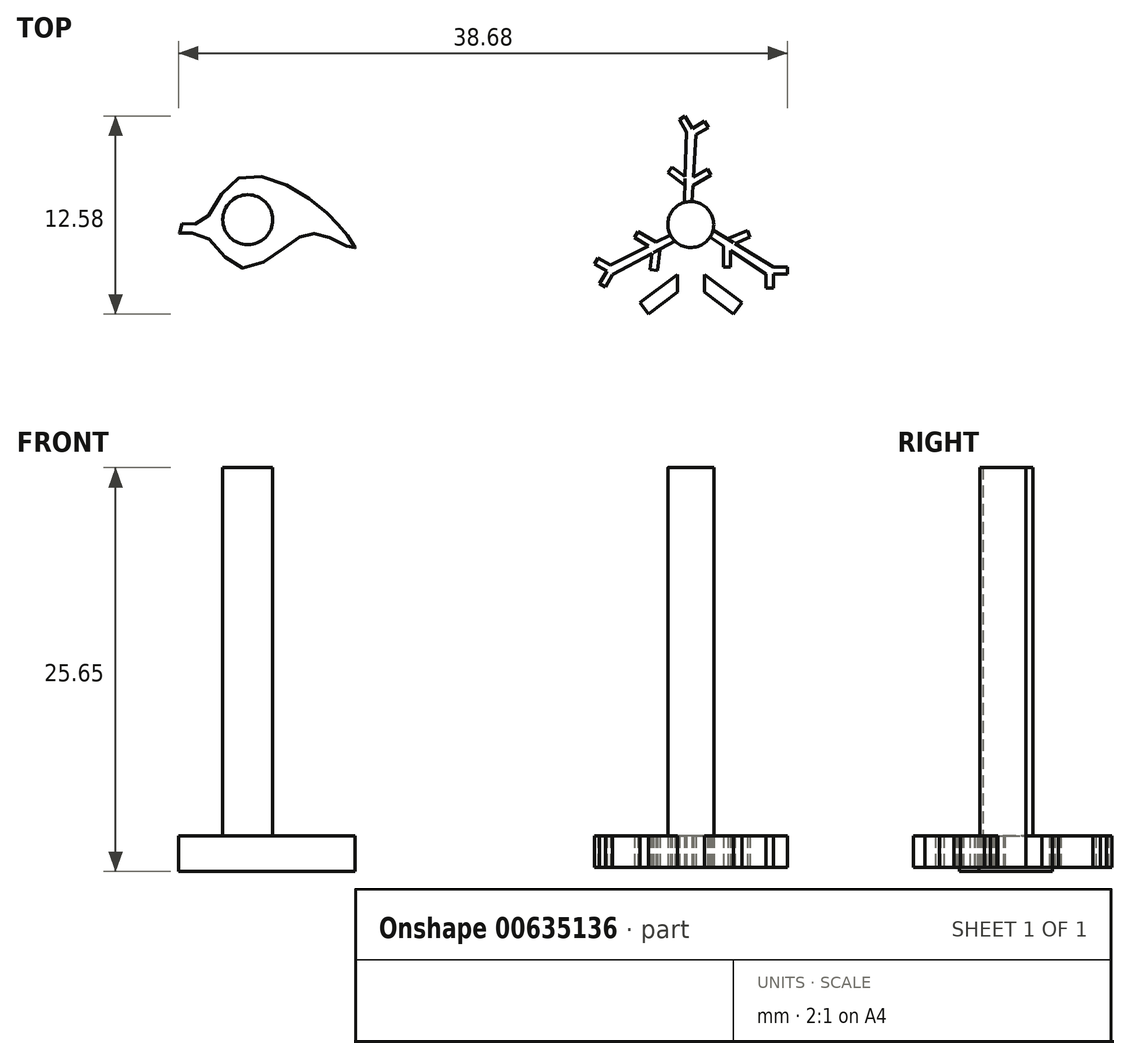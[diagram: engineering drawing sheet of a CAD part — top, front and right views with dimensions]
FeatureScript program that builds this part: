
annotation { "Feature Type Name" : "Feature", "Feature Type Description" : "" }
export const myFeature = defineFeature(function(context is Context, id is Id, definition is map)
    precondition{}
    {
        {
            var Q0;
            Q0=qCreatedBy(makeId("Top.planeOp"),FACE);
            var sketch = newSketch(context, id + "F0", { "sketchPlane" : qUnion([Q0])});
            skLineSegment(sketch, "E0.bottom", {"start": v(-0.85, 0) * mm, "end": v(0.86, 0) * mm});
            skLineSegment(sketch, "E0.top", {"start": v(-0.85, -6.35) * mm, "end": v(0.86, -6.35) * mm});
            skLineSegment(sketch, "E0.left", {"start": v(-0.85, 0) * mm, "end": v(-0.85, -6.35) * mm});
            skLineSegment(sketch, "E0.right", {"start": v(0.86, 0) * mm, "end": v(0.86, -6.35) * mm});
            skLineSegment(sketch, "E1", {"start": v(-0.85, -3.17) * mm, "end": v(-3.24, -4.96) * mm});
            skLineSegment(sketch, "E2", {"start": v(-3.24, -4.96) * mm, "end": v(-2.7, -5.69) * mm});
            skLineSegment(sketch, "E3", {"start": v(-2.7, -5.69) * mm, "end": v(-0.85, -4.3) * mm});
            skLineSegment(sketch, "E4", {"start": v(-0.85, -4.3) * mm, "end": v(-0.85, -3.17) * mm});
            skLineSegment(sketch, "E5", {"start": v(0, 0) * mm, "end": v(0, -6.35) * mm, "construction": true});
            skLineSegment(sketch, "E6.MirrorCS", {"start": v(2.71, -5.69) * mm, "end": v(0.86, -4.3) * mm});
            skLineSegment(sketch, "E7.MirrorCS", {"start": v(3.25, -4.96) * mm, "end": v(2.71, -5.69) * mm});
            skLineSegment(sketch, "E8.MirrorCS", {"start": v(0.86, -3.17) * mm, "end": v(3.25, -4.96) * mm});
            skLineSegment(sketch, "E9.MirrorCS", {"start": v(0.86, -4.3) * mm, "end": v(0.86, -3.17) * mm});
            skLineSegment(sketch, "E10.MirrorCS", {"start": v(0.86, 0) * mm, "end": v(-0.85, 0) * mm});
            skLineSegment(sketch, "E11.MirrorCS", {"start": v(0.86, -6.35) * mm, "end": v(-0.85, -6.35) * mm});
            skLineSegment(sketch, "E12", {"start": v(0, 0) * mm, "end": v(4.78, -3.14) * mm});
            skLineSegment(sketch, "E13", {"start": v(4.78, -3.14) * mm, "end": v(4.78, -4.05) * mm});
            skLineSegment(sketch, "E14", {"start": v(4.78, -4.05) * mm, "end": v(5.24, -4.05) * mm});
            skLineSegment(sketch, "E15", {"start": v(5.24, -4.05) * mm, "end": v(5.24, -3.14) * mm});
            skLineSegment(sketch, "E16", {"start": v(5.24, -3.14) * mm, "end": v(6.15, -3.14) * mm});
            skLineSegment(sketch, "E17", {"start": v(6.15, -3.14) * mm, "end": v(6.15, -2.7) * mm});
            skLineSegment(sketch, "E18", {"start": v(6.15, -2.7) * mm, "end": v(5.24, -2.7) * mm});
            skLineSegment(sketch, "E19", {"start": v(5.24, -2.7) * mm, "end": v(0.86, 0) * mm});
            skLineSegment(sketch, "E20", {"start": v(2.06, -1.35) * mm, "end": v(2.06, -2.68) * mm});
            skLineSegment(sketch, "E21", {"start": v(2.06, -2.68) * mm, "end": v(2.52, -2.68) * mm});
            skLineSegment(sketch, "E22", {"start": v(2.52, -2.68) * mm, "end": v(2.52, -1.65) * mm});
            skLineSegment(sketch, "E23", {"start": v(0.51, 0) * mm, "end": v(5.24, -3.14) * mm, "construction": true});
            skLineSegment(sketch, "E24.MirrorCS", {"start": v(3.76, -0.8) * mm, "end": v(2.8, -1.2) * mm});
            skLineSegment(sketch, "E25.MirrorCS", {"start": v(3.59, -0.39) * mm, "end": v(3.76, -0.8) * mm});
            skLineSegment(sketch, "E26.MirrorCS", {"start": v(2.36, -0.9) * mm, "end": v(3.59, -0.39) * mm});
            skLineSegment(sketch, "E27", {"start": v(2.36, -0.9) * mm, "end": v(2.8, -1.2) * mm});
            skLineSegment(sketch, "E28.1.0", {"start": v(0.33, 5.71) * mm, "end": v(1.11, 6.17) * mm});
            skLineSegment(sketch, "E28.1.1", {"start": v(0, 0) * mm, "end": v(5.5, 3.18) * mm, "construction": true});
            skLineSegment(sketch, "E28.1.2", {"start": v(2.32, 2.34) * mm, "end": v(2.67, 5.3) * mm});
            skLineSegment(sketch, "E28.1.3", {"start": v(0.14, 2.46) * mm, "end": v(1.3, 3.13) * mm});
            skLineSegment(sketch, "E28.1.4", {"start": v(1.07, 3.52) * mm, "end": v(0.17, 3) * mm});
            skLineSegment(sketch, "E28.1.5", {"start": v(3.57, 5.2) * mm, "end": v(3.3, 2.9) * mm});
            skLineSegment(sketch, "E28.1.6", {"start": v(-1.18, 3.66) * mm, "end": v(-0.36, 3.04) * mm});
            skLineSegment(sketch, "E28.1.7", {"start": v(-0.43, 0.75) * mm, "end": v(5.07, 3.92) * mm});
            skLineSegment(sketch, "E28.1.8", {"start": v(0, 0) * mm, "end": v(0.33, 5.71) * mm});
            skLineSegment(sketch, "E28.1.9", {"start": v(0.43, -0.74) * mm, "end": v(5.92, 2.44) * mm});
            skLineSegment(sketch, "E28.1.10", {"start": v(-0.4, 2.5) * mm, "end": v(-1.46, 3.3) * mm});
            skLineSegment(sketch, "E28.1.11", {"start": v(3.3, 2.9) * mm, "end": v(2.32, 2.34) * mm});
            skLineSegment(sketch, "E28.1.12", {"start": v(2.67, 5.3) * mm, "end": v(3.57, 5.2) * mm});
            skLineSegment(sketch, "E28.1.13", {"start": v(-0.26, 0.44) * mm, "end": v(0.1, 6.1) * mm, "construction": true});
            skLineSegment(sketch, "E28.1.14", {"start": v(3.18, 0.85) * mm, "end": v(5.92, -0.33) * mm});
            skLineSegment(sketch, "E28.1.15", {"start": v(0.1, 6.1) * mm, "end": v(-0.36, 6.9) * mm});
            skLineSegment(sketch, "E28.1.16", {"start": v(-0.28, 5.89) * mm, "end": v(-0.43, 0.75) * mm});
            skLineSegment(sketch, "E28.1.17", {"start": v(0.88, 6.56) * mm, "end": v(0.1, 6.1) * mm});
            skLineSegment(sketch, "E28.1.18", {"start": v(0.43, -0.74) * mm, "end": v(-0.43, 0.75) * mm});
            skLineSegment(sketch, "E28.1.19", {"start": v(5.92, 2.44) * mm, "end": v(5.07, 3.92) * mm});
            skLineSegment(sketch, "E28.1.20", {"start": v(5.92, -0.33) * mm, "end": v(6.27, 0.5) * mm});
            skLineSegment(sketch, "E28.1.21", {"start": v(-0.73, 6.67) * mm, "end": v(-0.28, 5.89) * mm});
            skLineSegment(sketch, "E28.1.22", {"start": v(6.27, 0.5) * mm, "end": v(4.15, 1.41) * mm});
            skLineSegment(sketch, "E28.1.23", {"start": v(5.92, -0.33) * mm, "end": v(6.27, 0.5) * mm});
            skLineSegment(sketch, "E28.1.24", {"start": v(3.57, 5.2) * mm, "end": v(3.3, 2.9) * mm});
            skLineSegment(sketch, "E28.1.25", {"start": v(6.27, 0.5) * mm, "end": v(4.15, 1.41) * mm});
            skLineSegment(sketch, "E28.1.26", {"start": v(2.67, 5.3) * mm, "end": v(3.57, 5.2) * mm});
            skLineSegment(sketch, "E28.1.27", {"start": v(4.15, 1.41) * mm, "end": v(3.18, 0.85) * mm});
            skLineSegment(sketch, "E28.1.28", {"start": v(-0.43, 0.75) * mm, "end": v(0.43, -0.74) * mm});
            skLineSegment(sketch, "E28.1.29", {"start": v(2.32, 2.34) * mm, "end": v(2.67, 5.3) * mm});
            skLineSegment(sketch, "E28.1.30", {"start": v(5.07, 3.92) * mm, "end": v(5.92, 2.44) * mm});
            skLineSegment(sketch, "E28.1.31", {"start": v(-0.43, 0.75) * mm, "end": v(5.07, 3.92) * mm});
            skLineSegment(sketch, "E28.1.32", {"start": v(3.18, 0.85) * mm, "end": v(5.92, -0.33) * mm});
            skLineSegment(sketch, "E28.1.33", {"start": v(3.3, 2.9) * mm, "end": v(2.32, 2.34) * mm});
            skLineSegment(sketch, "E28.1.34", {"start": v(0.43, -0.74) * mm, "end": v(5.92, 2.44) * mm});
            skLineSegment(sketch, "E28.1.35", {"start": v(4.15, 1.41) * mm, "end": v(3.18, 0.85) * mm});
            skLineSegment(sketch, "E28.1.36", {"start": v(1.3, 3.13) * mm, "end": v(1.07, 3.52) * mm});
            skLineSegment(sketch, "E28.1.37", {"start": v(-0.4, 2.5) * mm, "end": v(-0.36, 3.04) * mm});
            skLineSegment(sketch, "E28.1.38", {"start": v(1.11, 6.17) * mm, "end": v(0.88, 6.56) * mm});
            skLineSegment(sketch, "E28.1.39", {"start": v(-0.36, 6.9) * mm, "end": v(-0.73, 6.67) * mm});
            skLineSegment(sketch, "E28.1.40", {"start": v(-1.46, 3.3) * mm, "end": v(-1.18, 3.66) * mm});
            skLineSegment(sketch, "E28.2.0", {"start": v(-5.1, -2.57) * mm, "end": v(-5.9, -2.12) * mm});
            skLineSegment(sketch, "E28.2.1", {"start": v(0, 0) * mm, "end": v(-5.5, 3.17) * mm, "construction": true});
            skLineSegment(sketch, "E28.2.2", {"start": v(-3.18, 0.84) * mm, "end": v(-5.93, -0.34) * mm});
            skLineSegment(sketch, "E28.2.3", {"start": v(-2.2, -1.11) * mm, "end": v(-3.36, -0.44) * mm});
            skLineSegment(sketch, "E28.2.4", {"start": v(-3.58, -0.84) * mm, "end": v(-2.69, -1.36) * mm});
            skLineSegment(sketch, "E28.2.5", {"start": v(-6.28, 0.5) * mm, "end": v(-4.16, 1.4) * mm});
            skLineSegment(sketch, "E28.2.6", {"start": v(-2.58, -2.86) * mm, "end": v(-2.45, -1.83) * mm});
            skLineSegment(sketch, "E28.2.7", {"start": v(-0.43, -0.75) * mm, "end": v(-5.93, 2.43) * mm});
            skLineSegment(sketch, "E28.2.8", {"start": v(0, 0) * mm, "end": v(-5.1, -2.57) * mm});
            skLineSegment(sketch, "E28.2.9", {"start": v(0.43, 0.74) * mm, "end": v(-5.07, 3.91) * mm});
            skLineSegment(sketch, "E28.2.10", {"start": v(-1.96, -1.6) * mm, "end": v(-2.13, -2.91) * mm});
            skLineSegment(sketch, "E28.2.11", {"start": v(-4.16, 1.4) * mm, "end": v(-3.18, 0.84) * mm});
            skLineSegment(sketch, "E28.2.12", {"start": v(-5.93, -0.34) * mm, "end": v(-6.28, 0.5) * mm});
            skLineSegment(sketch, "E28.2.13", {"start": v(-0.26, -0.44) * mm, "end": v(-5.34, -2.97) * mm, "construction": true});
            skLineSegment(sketch, "E28.2.14", {"start": v(-2.32, 2.32) * mm, "end": v(-2.68, 5.29) * mm});
            skLineSegment(sketch, "E28.2.15", {"start": v(-5.34, -2.97) * mm, "end": v(-5.8, -3.75) * mm});
            skLineSegment(sketch, "E28.2.16", {"start": v(-4.96, -3.18) * mm, "end": v(-0.43, -0.75) * mm});
            skLineSegment(sketch, "E28.2.17", {"start": v(-6.12, -2.51) * mm, "end": v(-5.34, -2.97) * mm});
            skLineSegment(sketch, "E28.2.18", {"start": v(0.43, 0.74) * mm, "end": v(-0.43, -0.75) * mm});
            skLineSegment(sketch, "E28.2.19", {"start": v(-5.07, 3.91) * mm, "end": v(-5.93, 2.43) * mm});
            skLineSegment(sketch, "E28.2.20", {"start": v(-2.68, 5.29) * mm, "end": v(-3.57, 5.18) * mm});
            skLineSegment(sketch, "E28.2.21", {"start": v(-5.41, -3.97) * mm, "end": v(-4.96, -3.18) * mm});
            skLineSegment(sketch, "E28.2.22", {"start": v(-3.57, 5.18) * mm, "end": v(-3.3, 2.89) * mm});
            skLineSegment(sketch, "E28.2.23", {"start": v(-2.68, 5.29) * mm, "end": v(-3.57, 5.18) * mm});
            skLineSegment(sketch, "E28.2.24", {"start": v(-6.28, 0.5) * mm, "end": v(-4.16, 1.4) * mm});
            skLineSegment(sketch, "E28.2.25", {"start": v(-3.57, 5.18) * mm, "end": v(-3.3, 2.89) * mm});
            skLineSegment(sketch, "E28.2.26", {"start": v(-5.93, -0.34) * mm, "end": v(-6.28, 0.5) * mm});
            skLineSegment(sketch, "E28.2.27", {"start": v(-3.3, 2.89) * mm, "end": v(-2.32, 2.32) * mm});
            skLineSegment(sketch, "E28.2.28", {"start": v(-0.43, -0.75) * mm, "end": v(0.43, 0.74) * mm});
            skLineSegment(sketch, "E28.2.29", {"start": v(-3.18, 0.84) * mm, "end": v(-5.93, -0.34) * mm});
            skLineSegment(sketch, "E28.2.30", {"start": v(-5.93, 2.43) * mm, "end": v(-5.07, 3.91) * mm});
            skLineSegment(sketch, "E28.2.31", {"start": v(-0.43, -0.75) * mm, "end": v(-5.93, 2.43) * mm});
            skLineSegment(sketch, "E28.2.32", {"start": v(-2.32, 2.32) * mm, "end": v(-2.68, 5.29) * mm});
            skLineSegment(sketch, "E28.2.33", {"start": v(-4.16, 1.4) * mm, "end": v(-3.18, 0.84) * mm});
            skLineSegment(sketch, "E28.2.34", {"start": v(0.43, 0.74) * mm, "end": v(-5.07, 3.91) * mm});
            skLineSegment(sketch, "E28.2.35", {"start": v(-3.3, 2.89) * mm, "end": v(-2.32, 2.32) * mm});
            skLineSegment(sketch, "E28.2.36", {"start": v(-3.36, -0.44) * mm, "end": v(-3.58, -0.84) * mm});
            skLineSegment(sketch, "E28.2.37", {"start": v(-1.96, -1.6) * mm, "end": v(-2.45, -1.83) * mm});
            skLineSegment(sketch, "E28.2.38", {"start": v(-5.9, -2.12) * mm, "end": v(-6.12, -2.51) * mm});
            skLineSegment(sketch, "E28.2.39", {"start": v(-5.8, -3.75) * mm, "end": v(-5.41, -3.97) * mm});
            skLineSegment(sketch, "E28.2.40", {"start": v(-2.13, -2.91) * mm, "end": v(-2.58, -2.86) * mm});
            skPoint(sketch, "E28.center", {"position": v(0, 0) * mm});
            skSolve(sketch);
        }
        {
            var Q0;
            Q0=qCreatedBy(makeId("Top.planeOp"),FACE);
            var sketch = newSketch(context, id + "F1", { "sketchPlane" : qUnion([Q0])});
            skCircle(sketch, "E29", {"center": v(0, 0) * mm, "radius": 1.46 * mm});
            skSolve(sketch);
        }
        {
            var Q0;
            {var subQ9=sQuery(id+"F0.wireOp",EDGE,"E28.1.0");Q0=makeQuery(id+"F0.imprint","IMPRINT",FACE,{"disambiguationData":[TD([[makeQuery(id+"F0.imprint","IMPRINT",EDGE,{"derivedFrom":subQ9}),1.0]])]});}
            var Q1;
            {var subQ9=sQuery(id+"F0.wireOp",EDGE,"E28.2.0");Q1=makeQuery(id+"F0.imprint","IMPRINT",FACE,{"disambiguationData":[TD([[makeQuery(id+"F0.imprint","IMPRINT",EDGE,{"derivedFrom":subQ9}),1.0]])]});}
            var Q2;
            {var subQ8=sQuery(id+"F0.wireOp",EDGE,"E28.1.30");Q2=makeQuery(id+"F0.imprint","IMPRINT",FACE,{"disambiguationData":[TD([[makeQuery(id+"F0.imprint","IMPRINT",EDGE,{"derivedFrom":subQ8}),-1.0]])]});}
            var Q3;
            {var subQ10=sQuery(id+"F0.wireOp",EDGE,"E11.MirrorCS");Q3=makeQuery(id+"F0.imprint","IMPRINT",FACE,{"disambiguationData":[TD([[makeQuery(id+"F0.imprint","IMPRINT",EDGE,{"derivedFrom":subQ10}),-1.0]])]});}
            var Q4;
            {var subQ0=sQuery(id+"F0.wireOp",EDGE,"E1");Q4=makeQuery(id+"F0.imprint","IMPRINT",FACE,{"disambiguationData":[TD([[makeQuery(id+"F0.imprint","IMPRINT",EDGE,{"derivedFrom":subQ0}),1.0]])]});}
            var Q5;
            Q5=makeQuery(id+"F0.imprint","IMPRINT",FACE,{"disambiguationData":[TD([[makeQuery(id+"F0.imprint","IMPRINT",EDGE,{"derivedFrom":sQuery(id+"F0.wireOp",EDGE,"E8.MirrorCS")}),-1.0]])]});
            var Q6;
            {var subQ0=sQuery(id+"F0.wireOp",EDGE,"E20");Q6=makeQuery(id+"F0.imprint","IMPRINT",FACE,{"disambiguationData":[TD([[makeQuery(id+"F0.imprint","IMPRINT",EDGE,{"derivedFrom":subQ0}),1.0]])]});}
            var Q7;
            {var subQ1=sQuery(id+"F0.wireOp",EDGE,"E25.MirrorCS");Q7=makeQuery(id+"F0.imprint","IMPRINT",FACE,{"disambiguationData":[TD([[makeQuery(id+"F0.imprint","IMPRINT",EDGE,{"derivedFrom":subQ1}),-1.0]])]});}
            var Q8;
            {var subQ0=sQuery(id+"F0.wireOp",EDGE,"E28.1.3");Q8=makeQuery(id+"F0.imprint","IMPRINT",FACE,{"disambiguationData":[TD([[makeQuery(id+"F0.imprint","IMPRINT",EDGE,{"derivedFrom":subQ0}),1.0]])]});}
            var Q9;
            {var subQ1=sQuery(id+"F0.wireOp",EDGE,"E28.1.10");Q9=makeQuery(id+"F0.imprint","IMPRINT",FACE,{"disambiguationData":[TD([[makeQuery(id+"F0.imprint","IMPRINT",EDGE,{"derivedFrom":subQ1}),-1.0]])]});}
            var Q10;
            Q10=makeQuery(id+"F0.imprint","IMPRINT",FACE,{"disambiguationData":[TD([[makeQuery(id+"F0.imprint","IMPRINT",EDGE,{"derivedFrom":sQuery(id+"F0.wireOp",EDGE,"E28.1.23")}),1.0]])]});
            var Q11;
            Q11=makeQuery(id+"F0.imprint","IMPRINT",FACE,{"disambiguationData":[TD([[makeQuery(id+"F0.imprint","IMPRINT",EDGE,{"derivedFrom":sQuery(id+"F0.wireOp",EDGE,"E28.1.24")}),-1.0]])]});
            var Q12;
            {var subQ0=sQuery(id+"F0.wireOp",EDGE,"E28.2.3");Q12=makeQuery(id+"F0.imprint","IMPRINT",FACE,{"disambiguationData":[TD([[makeQuery(id+"F0.imprint","IMPRINT",EDGE,{"derivedFrom":subQ0}),1.0]])]});}
            var Q13;
            {var subQ1=sQuery(id+"F0.wireOp",EDGE,"E28.2.10");Q13=makeQuery(id+"F0.imprint","IMPRINT",FACE,{"disambiguationData":[TD([[makeQuery(id+"F0.imprint","IMPRINT",EDGE,{"derivedFrom":subQ1}),-1.0]])]});}
            var Q14;
            Q14=makeQuery(id+"F0.imprint","IMPRINT",FACE,{"disambiguationData":[TD([[makeQuery(id+"F0.imprint","IMPRINT",EDGE,{"derivedFrom":sQuery(id+"F0.wireOp",EDGE,"E28.2.23")}),1.0]])]});
            var Q15;
            Q15=makeQuery(id+"F0.imprint","IMPRINT",FACE,{"disambiguationData":[TD([[makeQuery(id+"F0.imprint","IMPRINT",EDGE,{"derivedFrom":sQuery(id+"F0.wireOp",EDGE,"E28.2.24")}),-1.0]])]});
            var Q16;
            {var subQ1=sQuery(id+"F0.wireOp",EDGE,"E10.MirrorCS");var subQ3=sQuery(id+"F0.wireOp",EDGE,"E12");var subQ4=makeQuery(id+"F0.imprint","INTERSECT",VERTEX,{"derivedFrom":[subQ1,subQ3]});Q16=makeQuery(id+"F0.imprint","IMPRINT",FACE,{"disambiguationData":[TD([[makeQuery(id+"F0.imprint","IMPRINT",EDGE,{"disambiguationData":[TD([[subQ4,-1.0]])],"derivedFrom":subQ3}),1.0]])]});}
            var Q17;
            {var subQ2=sQuery(id+"F0.wireOp",EDGE,"E28.2.30");Q17=makeQuery(id+"F0.imprint","IMPRINT",FACE,{"disambiguationData":[TD([[makeQuery(id+"F0.imprint","IMPRINT",EDGE,{"derivedFrom":subQ2}),-1.0]])]});}
            var Q18;
            {var subQ6=sQuery(id+"F0.wireOp",EDGE,"E13");Q18=makeQuery(id+"F0.imprint","IMPRINT",FACE,{"disambiguationData":[TD([[makeQuery(id+"F0.imprint","IMPRINT",EDGE,{"derivedFrom":subQ6}),1.0]])]});}
            var Q19;
            {var subQ0=sQuery(id+"F0.wireOp",EDGE,"E12");var subQ1=sQuery(id+"F0.wireOp",EDGE,"E10.MirrorCS");var subQ2=makeQuery(id+"F0.imprint","INTERSECT",VERTEX,{"derivedFrom":[subQ1,subQ0]});Q19=makeQuery(id+"F0.imprint","IMPRINT",FACE,{"disambiguationData":[TD([[makeQuery(id+"F0.imprint","IMPRINT",EDGE,{"disambiguationData":[TD([[subQ2,-1.0]])],"derivedFrom":subQ0}),-1.0]])]});}
            var Q20;
            {var subQ0=sQuery(id+"F0.wireOp",EDGE,"E28.1.28");var subQ1=sQuery(id+"F0.wireOp",EDGE,"E28.1.8");var subQ2=makeQuery(id+"F0.imprint","INTERSECT",VERTEX,{"derivedFrom":[subQ1,subQ0]});Q20=makeQuery(id+"F0.imprint","IMPRINT",FACE,{"disambiguationData":[TD([[makeQuery(id+"F0.imprint","IMPRINT",EDGE,{"disambiguationData":[TD([[subQ2,-1.0]])],"derivedFrom":subQ1}),1.0]])]});}
            var Q21;
            {var subQ0=sQuery(id+"F0.wireOp",EDGE,"E28.1.28");var subQ1=sQuery(id+"F0.wireOp",EDGE,"E28.1.8");var subQ2=makeQuery(id+"F0.imprint","INTERSECT",VERTEX,{"derivedFrom":[subQ1,subQ0]});Q21=makeQuery(id+"F0.imprint","IMPRINT",FACE,{"disambiguationData":[TD([[makeQuery(id+"F0.imprint","IMPRINT",EDGE,{"disambiguationData":[TD([[subQ2,-1.0]])],"derivedFrom":subQ1}),-1.0]])]});}
            var Q22;
            {var subQ0=sQuery(id+"F0.wireOp",EDGE,"E28.2.8");var subQ1=sQuery(id+"F0.wireOp",EDGE,"E0.left");var subQ2=makeQuery(id+"F0.imprint","INTERSECT",VERTEX,{"derivedFrom":[subQ1,subQ0]});Q22=makeQuery(id+"F0.imprint","IMPRINT",FACE,{"disambiguationData":[TD([[makeQuery(id+"F0.imprint","IMPRINT",EDGE,{"disambiguationData":[TD([[subQ2,-1.0]])],"derivedFrom":subQ1}),1.0]])]});}
            var Q23;
            {var subQ0=sQuery(id+"F0.wireOp",EDGE,"E0.left");var subQ1=sQuery(id+"F0.wireOp",EDGE,"E10.MirrorCS");var subQ2=makeQuery(id+"F0.imprint","INTERSECT",VERTEX,{"derivedFrom":[subQ1,subQ0]});Q23=makeQuery(id+"F0.imprint","IMPRINT",FACE,{"disambiguationData":[TD([[makeQuery(id+"F0.imprint","IMPRINT",EDGE,{"disambiguationData":[TD([[subQ2,-1.0]])],"derivedFrom":subQ0}),1.0]])]});}
            var Q24;
            {var subQ0=sQuery(id+"F0.wireOp",EDGE,"E19");var subQ3=sQuery(id+"F0.wireOp",EDGE,"E28.1.34");var subQ5=makeQuery(id+"F0.imprint","INTERSECT",VERTEX,{"derivedFrom":[subQ0,subQ3]});Q24=makeQuery(id+"F0.imprint","IMPRINT",FACE,{"disambiguationData":[TD([[makeQuery(id+"F0.imprint","IMPRINT",EDGE,{"disambiguationData":[TD([[subQ5,1.0]])],"derivedFrom":subQ3}),1.0]])]});}
            var Q25;
            {var subQ0=sQuery(id+"F0.wireOp",EDGE,"E28.2.16");var subQ1=sQuery(id+"F0.wireOp",EDGE,"E0.left");var subQ2=makeQuery(id+"F0.imprint","INTERSECT",VERTEX,{"derivedFrom":[subQ1,subQ0]});Q25=makeQuery(id+"F0.imprint","IMPRINT",FACE,{"disambiguationData":[TD([[makeQuery(id+"F0.imprint","IMPRINT",EDGE,{"disambiguationData":[TD([[subQ2,1.0]])],"derivedFrom":subQ1}),1.0]])]});}
            var Q26;
            {var subQ0=sQuery(id+"F0.wireOp",EDGE,"E28.1.31");var subQ1=sQuery(id+"F0.wireOp",EDGE,"E28.1.8");var subQ2=makeQuery(id+"F0.imprint","INTERSECT",VERTEX,{"derivedFrom":[subQ1,subQ0]});Q26=makeQuery(id+"F0.imprint","IMPRINT",FACE,{"disambiguationData":[TD([[makeQuery(id+"F0.imprint","IMPRINT",EDGE,{"disambiguationData":[TD([[subQ2,1.0]])],"derivedFrom":subQ1}),1.0]])]});}
            var Q27;
            {var subQ0=sQuery(id+"F0.wireOp",EDGE,"E28.2.8");var subQ1=sQuery(id+"F0.wireOp",EDGE,"E0.left");var subQ2=makeQuery(id+"F0.imprint","INTERSECT",VERTEX,{"derivedFrom":[subQ1,subQ0]});Q27=makeQuery(id+"F0.imprint","IMPRINT",FACE,{"disambiguationData":[TD([[makeQuery(id+"F0.imprint","IMPRINT",EDGE,{"disambiguationData":[TD([[subQ2,-1.0]])],"derivedFrom":subQ1}),-1.0]])]});}
            var Q28;
            {var subQ0=sQuery(id+"F0.wireOp",EDGE,"E28.1.37");var subQ1=sQuery(id+"F0.wireOp",EDGE,"E28.1.6");var subQ2=makeQuery(id+"F0.imprint","INTERSECT",VERTEX,{"derivedFrom":[subQ1,subQ0]});Q28=makeQuery(id+"F0.imprint","IMPRINT",FACE,{"disambiguationData":[TD([[makeQuery(id+"F0.imprint","IMPRINT",EDGE,{"disambiguationData":[TD([[subQ2,1.0]])],"derivedFrom":subQ1}),-1.0]])]});}
            var Q29;
            {var subQ0=sQuery(id+"F0.wireOp",EDGE,"E24.MirrorCS");var subQ1=sQuery(id+"F0.wireOp",EDGE,"E19");var subQ2=makeQuery(id+"F0.imprint","INTERSECT",VERTEX,{"derivedFrom":[subQ1,subQ0]});Q29=makeQuery(id+"F0.imprint","IMPRINT",FACE,{"disambiguationData":[TD([[makeQuery(id+"F0.imprint","IMPRINT",EDGE,{"disambiguationData":[TD([[subQ2,-1.0]])],"derivedFrom":subQ1}),1.0]])]});}
            var Q30;
            {var subQ1=sQuery(id+"F0.wireOp",EDGE,"E28.1.16");var subQ3=sQuery(id+"F0.wireOp",EDGE,"E28.2.34");var subQ4=makeQuery(id+"F0.imprint","INTERSECT",VERTEX,{"derivedFrom":[subQ1,subQ3]});Q30=makeQuery(id+"F0.imprint","IMPRINT",FACE,{"disambiguationData":[TD([[makeQuery(id+"F0.imprint","IMPRINT",EDGE,{"disambiguationData":[TD([[subQ4,1.0]])],"derivedFrom":subQ3}),1.0]])]});}
            var Q31;
            {var subQ0=sQuery(id+"F0.wireOp",EDGE,"E12");var subQ1=sQuery(id+"F0.wireOp",EDGE,"E0.right");var subQ2=makeQuery(id+"F0.imprint","INTERSECT",VERTEX,{"derivedFrom":[subQ1,subQ0]});Q31=makeQuery(id+"F0.imprint","IMPRINT",FACE,{"disambiguationData":[TD([[makeQuery(id+"F0.imprint","IMPRINT",EDGE,{"disambiguationData":[TD([[subQ2,1.0]])],"derivedFrom":subQ1}),-1.0]])]});}
            var Q32;
            {var subQ0=sQuery(id+"F0.wireOp",EDGE,"E28.2.37");var subQ1=sQuery(id+"F0.wireOp",EDGE,"E28.2.6");var subQ2=makeQuery(id+"F0.imprint","INTERSECT",VERTEX,{"derivedFrom":[subQ1,subQ0]});Q32=makeQuery(id+"F0.imprint","IMPRINT",FACE,{"disambiguationData":[TD([[makeQuery(id+"F0.imprint","IMPRINT",EDGE,{"disambiguationData":[TD([[subQ2,1.0]])],"derivedFrom":subQ1}),-1.0]])]});}
            extrude(context, id + "F2", {"entities" : qUnion([Q0, Q1, Q2, Q3, Q4, Q5, Q6, Q7, Q8, Q9, Q10, Q11, Q12, Q13, Q14, Q15, Q16, Q17, Q18, Q19, Q20, Q21, Q22, Q23, Q24, Q25, Q26, Q27, Q28, Q29, Q30, Q31, Q32]), "depth" : 2 * mm, "offsetDistance" : 25.4 * mm});
        }
        {
            var Q0;
            Q0=makeQuery(id+"F1.imprint","IMPRINT",FACE,{"disambiguationData":[TD([[makeQuery(id+"F1.imprint","IMPRINT",EDGE,{"derivedFrom":sQuery(id+"F1.wireOp",EDGE,"E29")}),1.0]])]});
            extrude(context, id + "F3", {"entities" : qUnion([Q0]), "operationType" : NewBodyOperationType.ADD, "depth" : 25.4 * mm, "offsetDistance" : 25.4 * mm});
        }
        {
            var Q0;
            Q0=qCreatedBy(makeId("Top.planeOp"),FACE);
            var sketch = newSketch(context, id + "F4", { "sketchPlane" : qUnion([Q0])});
            skFitSpline(sketch, "E30", {"points": [v(-29.87, 0.29) * mm, v(-29.34, 0.29) * mm, v(-28.46, 1.45) * mm, v(-26.9, 1.36) * mm, v(-25.63, 0.43) * mm, v(-25.25, 0) * mm, v(-24.99, -0.43) * mm, v(-25.5, -0.21) * mm, v(-26.25, 0) * mm, v(-27, -0.43) * mm, v(-28.3, -0.95) * mm, v(-29.34, 0) * mm, v(-29.94, 0) * mm, v(-29.87, 0.29) * mm]});
            skPoint(sketch, "E31", {"position": v(-27.65, 0.45) * mm});
            skSolve(sketch);
        }
        {
            var Q0;
            Q0=makeQuery(id+"F4.imprint","IMPRINT",FACE,{"disambiguationData":[TD([[makeQuery(id+"F4.imprint","IMPRINT",EDGE,{"derivedFrom":sQuery(id+"F4.wireOp",EDGE,"E30")}),-1.0]])]});
            extrude(context, id + "F5", {"entities" : qUnion([Q0]), "depth" : 1 * mm, "offsetDistance" : 25.4 * mm});
        }
        {
            var Q0;
            Q0=makeQuery(id+"F5.opExtrude","CAP_FACE",FACE,{"disambiguationData":[OSD([sQuery(id+"F4.wireOp",EDGE,"E30")])],"isStart":false});
            var sketch = newSketch(context, id + "F6", { "sketchPlane" : qUnion([Q0])});
            skPoint(sketch, "E32", {"position": v(-27.91, 0.45) * mm});
            skSolve(sketch);
        }
        {
            var Q0;
            Q0=makeQuery(id+"F5.opExtrude","SWEPT_BODY",BODY,{"disambiguationData":[OSD([sQuery(id+"F4.wireOp",EDGE,"E30")])]});
            var Q1;
            Q1=sQuery(id+"F6.wireOp",VERTEX,"E32");
            transform(context, id + "F7", {"entities" : qUnion([Q0]), "transformType" : TransformType.SCALE_UNIFORMLY, "scale" : 2.25, "scalePoint" : qUnion([Q1]), "makeCopy" : false});
        }
        {
            var Q0;
            Q0=makeQuery(id+"F5.opExtrude","SWEPT_BODY",BODY,{"disambiguationData":[OSD([sQuery(id+"F4.wireOp",EDGE,"E30")])]});
            transform(context, id + "F8", {"entities" : qUnion([Q0]), "transformType" : TransformType.TRANSLATION_3D, "dx" : 0 * mm, "dy" : 0 * mm, "dz" : 1 * mm, "makeCopy" : false});
        }
        {
            var Q0;
            Q0=qCreatedBy(makeId("Top.planeOp"),FACE);
            var sketch = newSketch(context, id + "F9", { "sketchPlane" : qUnion([Q0])});
            skCircle(sketch, "E33", {"center": v(-28.13, 0.3) * mm, "radius": 1.59 * mm});
            skSolve(sketch);
        }
        {
            var Q0;
            Q0=makeQuery(id+"F9.imprint","IMPRINT",FACE,{"disambiguationData":[TD([[makeQuery(id+"F9.imprint","IMPRINT",EDGE,{"derivedFrom":sQuery(id+"F9.wireOp",EDGE,"E33")}),1.0]])]});
            extrude(context, id + "F10", {"entities" : qUnion([Q0]), "operationType" : NewBodyOperationType.ADD, "depth" : 25.4 * mm, "offsetDistance" : 25.4 * mm});
        }
    });
